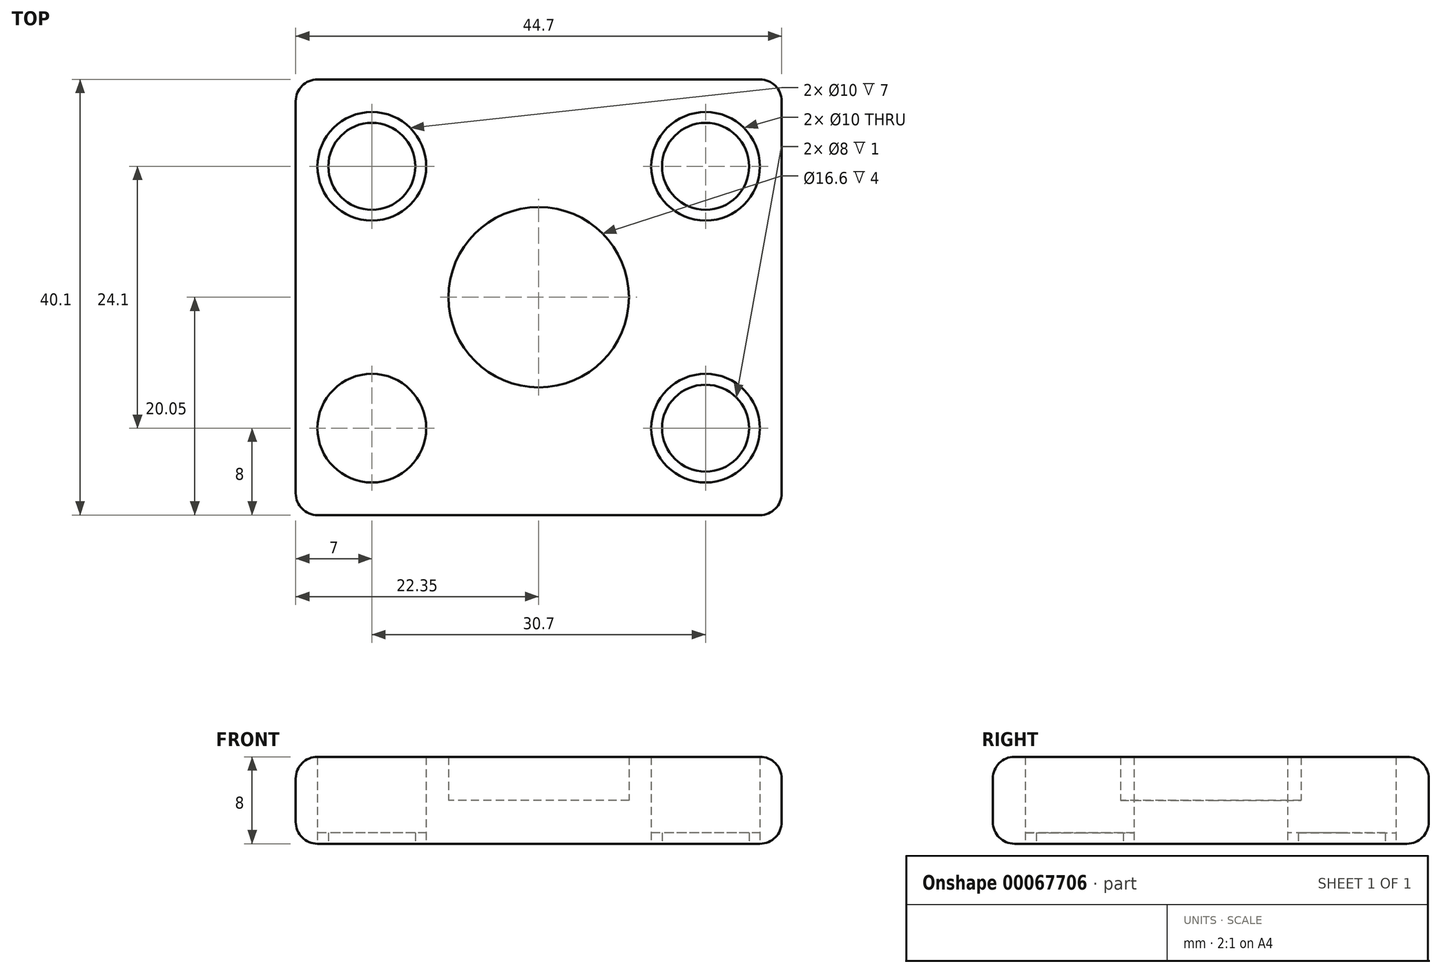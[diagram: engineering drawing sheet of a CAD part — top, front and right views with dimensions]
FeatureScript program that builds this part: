
annotation { "Feature Type Name" : "Feature", "Feature Type Description" : "" }
export const myFeature = defineFeature(function(context is Context, id is Id, definition is map)
    precondition{}
    {
        {
            var Q0;
            Q0=qCreatedBy(makeId("Top.planeOp"),FACE);
            var sketch = newSketch(context, id + "F0", { "sketchPlane" : qUnion([Q0])});
            skLineSegment(sketch, "E0.rect.bottom", {"start": v(-22.35, 20.05) * mm, "end": v(22.35, 20.05) * mm});
            skLineSegment(sketch, "E0.rect.top", {"start": v(-22.35, -20.05) * mm, "end": v(22.35, -20.05) * mm});
            skLineSegment(sketch, "E0.rect.left", {"start": v(-22.35, 20.05) * mm, "end": v(-22.35, -20.05) * mm});
            skLineSegment(sketch, "E0.rect.right", {"start": v(22.35, 20.05) * mm, "end": v(22.35, -20.05) * mm});
            skPoint(sketch, "E0.rect.middle", {"position": v(0, 0) * mm});
            skLineSegment(sketch, "E1", {"start": v(0, 20.05) * mm, "end": v(0, -20.05) * mm, "construction": true});
            skLineSegment(sketch, "E2", {"start": v(-22.35, 0) * mm, "end": v(22.35, 0) * mm, "construction": true});
            skCircle(sketch, "E3", {"center": v(-15.35, 12.05) * mm, "radius": 4 * mm});
            skCircle(sketch, "E4", {"center": v(-15.35, 12.05) * mm, "radius": 5 * mm});
            skCircle(sketch, "E5.MirrorC", {"center": v(15.35, 12.05) * mm, "radius": 4 * mm});
            skCircle(sketch, "E6.MirrorC", {"center": v(15.35, 12.05) * mm, "radius": 5 * mm});
            skLineSegment(sketch, "E7.MirrorCS", {"start": v(0, -20.05) * mm, "end": v(0, 20.05) * mm, "construction": true});
            skCircle(sketch, "E8.MirrorC", {"center": v(-15.35, -12.05) * mm, "radius": 5 * mm});
            skCircle(sketch, "E9.MirrorC", {"center": v(-15.35, -12.05) * mm, "radius": 4 * mm});
            skCircle(sketch, "E10.MirrorC", {"center": v(15.35, -12.05) * mm, "radius": 5 * mm});
            skCircle(sketch, "E11.MirrorC", {"center": v(15.35, -12.05) * mm, "radius": 4 * mm});
            skCircle(sketch, "E12", {"center": v(0, 0) * mm, "radius": 8.3 * mm});
            skSolve(sketch);
        }
        {
            var Q0;
            Q0=makeQuery(id+"F0.imprint","IMPRINT",FACE,{"disambiguationData":[TD([[makeQuery(id+"F0.imprint","IMPRINT",EDGE,{"derivedFrom":sQuery(id+"F0.wireOp",EDGE,"E0.rect.bottom")}),-1.0]])]});
            extrude(context, id + "F1", {"entities" : qUnion([Q0]), "depth" : 8 * mm});
        }
        {
            var Q0;
            Q0=makeQuery(id+"F0.imprint","IMPRINT",FACE,{"disambiguationData":[TD([[makeQuery(id+"F0.imprint","IMPRINT",EDGE,{"derivedFrom":sQuery(id+"F0.wireOp",EDGE,"E12")}),1.0]])]});
            extrude(context, id + "F2", {"entities" : qUnion([Q0]), "operationType" : NewBodyOperationType.ADD, "depth" : 4 * mm});
        }
        {
            var Q0;
            Q0=makeQuery(id+"F0.imprint","IMPRINT",FACE,{"disambiguationData":[TD([[makeQuery(id+"F0.imprint","IMPRINT",EDGE,{"derivedFrom":sQuery(id+"F0.wireOp",EDGE,"E5.MirrorC")}),1.0]])]});
            var Q1;
            Q1=makeQuery(id+"F0.imprint","IMPRINT",FACE,{"disambiguationData":[TD([[makeQuery(id+"F0.imprint","IMPRINT",EDGE,{"derivedFrom":sQuery(id+"F0.wireOp",EDGE,"E10.MirrorC")}),1.0]])]});
            var Q2;
            Q2=makeQuery(id+"F0.imprint","IMPRINT",FACE,{"disambiguationData":[TD([[makeQuery(id+"F0.imprint","IMPRINT",EDGE,{"derivedFrom":sQuery(id+"F0.wireOp",EDGE,"E8.MirrorC")}),-1.0]])]});
            var Q3;
            Q3=makeQuery(id+"F0.imprint","IMPRINT",FACE,{"disambiguationData":[TD([[makeQuery(id+"F0.imprint","IMPRINT",EDGE,{"derivedFrom":sQuery(id+"F0.wireOp",EDGE,"E3")}),-1.0]])]});
            extrude(context, id + "F3", {"entities" : qUnion([Q0, Q1, Q2, Q3]), "operationType" : NewBodyOperationType.ADD, "depth" : 1 * mm});
        }
        {
            var Q0;
            Q0=makeQuery(id+"F1.opExtrude","CAP_EDGE",EDGE,{"disambiguationData":[OSD([sQuery(id+"F0.wireOp",EDGE,"E0.rect.bottom")])],"isStart":false});
            var Q1;
            Q1=makeQuery(id+"F1.opExtrude","CAP_EDGE",EDGE,{"disambiguationData":[OSD([sQuery(id+"F0.wireOp",EDGE,"E0.rect.left")])],"isStart":false});
            var Q2;
            Q2=makeQuery(id+"F1.opExtrude","CAP_EDGE",EDGE,{"disambiguationData":[OSD([sQuery(id+"F0.wireOp",EDGE,"E0.rect.top")])],"isStart":false});
            var Q3;
            Q3=makeQuery(id+"F1.opExtrude","CAP_EDGE",EDGE,{"disambiguationData":[OSD([sQuery(id+"F0.wireOp",EDGE,"E0.rect.right")])],"isStart":false});
            var Q4;
            Q4=makeQuery(id+"F1.opExtrude","CAP_EDGE",EDGE,{"disambiguationData":[OSD([sQuery(id+"F0.wireOp",EDGE,"E0.rect.top")])],"isStart":true});
            var Q5;
            Q5=makeQuery(id+"F1.opExtrude","CAP_EDGE",EDGE,{"disambiguationData":[OSD([sQuery(id+"F0.wireOp",EDGE,"E0.rect.left")])],"isStart":true});
            var Q6;
            Q6=makeQuery(id+"F1.opExtrude","SWEPT_EDGE",EDGE,{"disambiguationData":[OSD([sQuery(id+"F0.wireOp",EDGE,"E0.rect.top"),sQuery(id+"F0.wireOp",EDGE,"E0.rect.left")])]});
            var Q7;
            Q7=makeQuery(id+"F1.opExtrude","SWEPT_EDGE",EDGE,{"disambiguationData":[OSD([sQuery(id+"F0.wireOp",EDGE,"E0.rect.top"),sQuery(id+"F0.wireOp",EDGE,"E0.rect.right")])]});
            var Q8;
            Q8=makeQuery(id+"F1.opExtrude","CAP_EDGE",EDGE,{"disambiguationData":[OSD([sQuery(id+"F0.wireOp",EDGE,"E0.rect.right")])],"isStart":true});
            var Q9;
            Q9=makeQuery(id+"F1.opExtrude","SWEPT_EDGE",EDGE,{"disambiguationData":[OSD([sQuery(id+"F0.wireOp",EDGE,"E0.rect.bottom"),sQuery(id+"F0.wireOp",EDGE,"E0.rect.right")])]});
            var Q10;
            Q10=makeQuery(id+"F1.opExtrude","CAP_EDGE",EDGE,{"disambiguationData":[OSD([sQuery(id+"F0.wireOp",EDGE,"E0.rect.bottom")])],"isStart":true});
            var Q11;
            Q11=makeQuery(id+"F1.opExtrude","SWEPT_EDGE",EDGE,{"disambiguationData":[OSD([sQuery(id+"F0.wireOp",EDGE,"E0.rect.bottom"),sQuery(id+"F0.wireOp",EDGE,"E0.rect.left")])]});
            fillet(context, id + "F4", {"entities" : qUnion([Q0, Q1, Q2, Q3, Q4, Q5, Q6, Q7, Q8, Q9, Q10, Q11]), "radius" : 2 * mm, "tangentPropagation" : true, "allowEdgeOverflow" : false});
        }
    });
